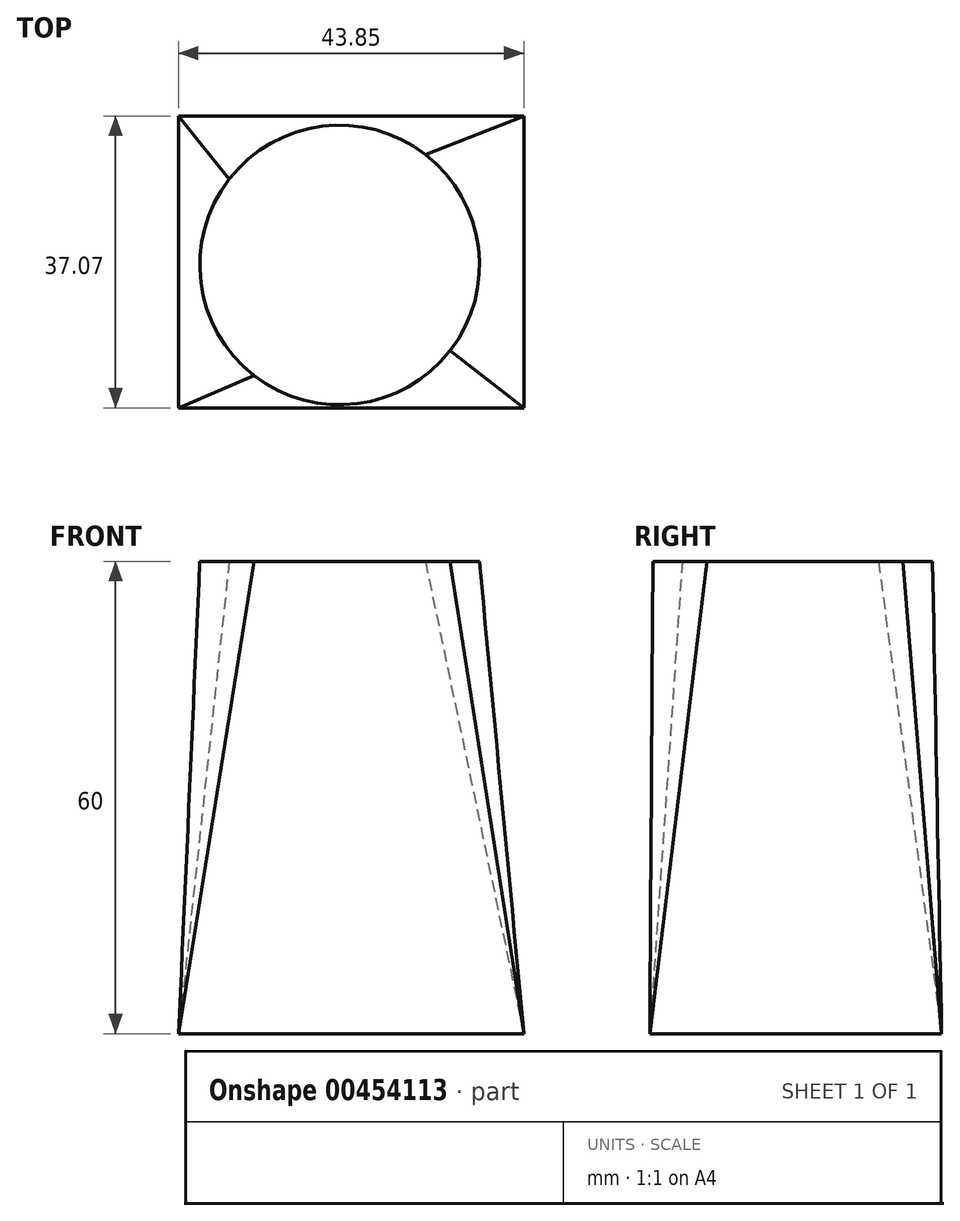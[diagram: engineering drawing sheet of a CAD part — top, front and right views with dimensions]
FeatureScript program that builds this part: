
annotation { "Feature Type Name" : "Feature", "Feature Type Description" : "" }
export const myFeature = defineFeature(function(context is Context, id is Id, definition is map)
    precondition{}
    {
        {
            var Q0;
            Q0=qCreatedBy(makeId("Top.planeOp"),FACE);
            var sketch = newSketch(context, id + "F0", { "sketchPlane" : qUnion([Q0])});
            skLineSegment(sketch, "E0.bottom", {"start": v(0, 0) * mm, "end": v(-43.85, 0) * mm});
            skLineSegment(sketch, "E0.top", {"start": v(0, 37.07) * mm, "end": v(-43.85, 37.07) * mm});
            skLineSegment(sketch, "E0.left", {"start": v(0, 0) * mm, "end": v(0, 37.07) * mm});
            skLineSegment(sketch, "E0.right", {"start": v(-43.85, 0) * mm, "end": v(-43.85, 37.07) * mm});
            skSolve(sketch);
        }
        {
            var Q0;
            Q0=qCreatedBy(makeId("Top.planeOp"),FACE);
            cPlane(context, id + "F1", {"entities" : qUnion([Q0]), "cplaneType" : CPlaneType.OFFSET, "offset" : 60 * mm, "width" : 150 * mm, "height" : 150 * mm});
        }
        {
            var Q0;
            Q0=qCreatedBy(id+"F1.planeOp",FACE);
            var sketch = newSketch(context, id + "F2", { "sketchPlane" : qUnion([Q0])});
            skCircle(sketch, "E1", {"center": v(-23.4, 18.15) * mm, "radius": 17.76 * mm});
            skSolve(sketch);
        }
        {
            var Q0;
            Q0 = qSketchRegion(id + "F2", true);
            var Q1;
            Q1 = qSketchRegion(id + "F0", true);
            loft(context, id + "F3", {"sheetProfilesArray" : [{ "sheetProfileEntities" : qUnion([Q0]) }, { "sheetProfileEntities" : qUnion([Q1]) }]});
        }
    });
